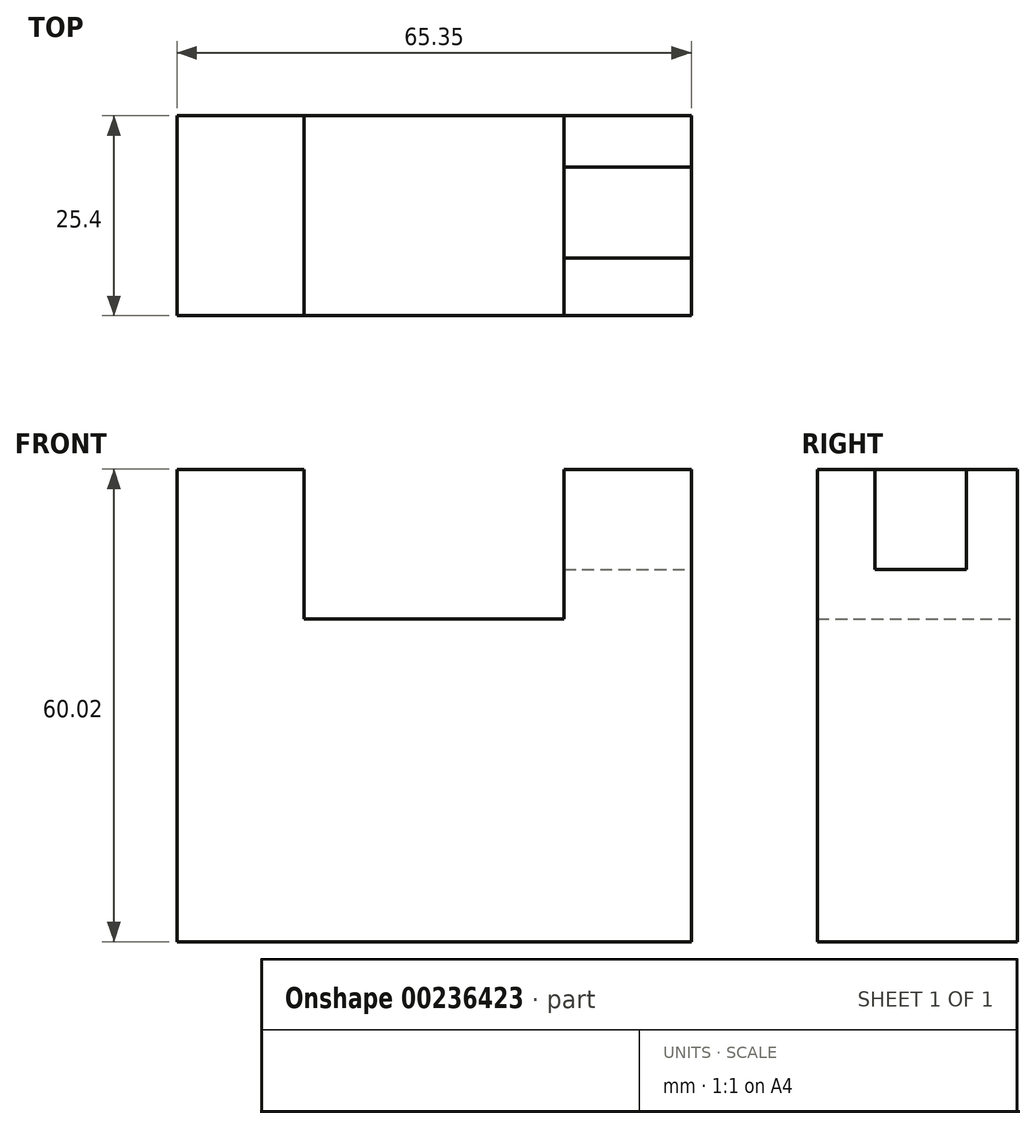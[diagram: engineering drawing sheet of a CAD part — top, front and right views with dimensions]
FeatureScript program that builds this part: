
annotation { "Feature Type Name" : "Feature", "Feature Type Description" : "" }
export const myFeature = defineFeature(function(context is Context, id is Id, definition is map)
    precondition{}
    {
        {
            var Q0;
            Q0=qCreatedBy(makeId("Front.planeOp"),FACE);
            var sketch = newSketch(context, id + "F0", { "sketchPlane" : qUnion([Q0])});
            skLineSegment(sketch, "E0.bottom", {"start": v(0, 0) * mm, "end": v(65.35, 0) * mm});
            skLineSegment(sketch, "E0.top", {"start": v(0, 60.02) * mm, "end": v(16.16, 60.02) * mm});
            skLineSegment(sketch, "E0.left", {"start": v(0, 0) * mm, "end": v(0, 60.02) * mm});
            skLineSegment(sketch, "E0.right", {"start": v(65.35, 0) * mm, "end": v(65.35, 60.02) * mm});
            skLineSegment(sketch, "E1.top", {"start": v(16.16, 40.99) * mm, "end": v(49.18, 40.99) * mm});
            skLineSegment(sketch, "E1.left", {"start": v(16.16, 60.02) * mm, "end": v(16.16, 40.99) * mm});
            skLineSegment(sketch, "E1.right", {"start": v(49.18, 60.02) * mm, "end": v(49.18, 40.99) * mm});
            skLineSegment(sketch, "E2.trimOffspring", {"start": v(49.18, 60.02) * mm, "end": v(65.35, 60.02) * mm});
            skSolve(sketch);
        }
        {
            var Q0;
            Q0=makeQuery(id+"F0.imprint","IMPRINT",FACE,{"disambiguationData":[TD([[makeQuery(id+"F0.imprint","IMPRINT",EDGE,{"derivedFrom":sQuery(id+"F0.wireOp",EDGE,"E0.bottom")}),1.0]])]});
            extrude(context, id + "F1", {"entities" : qUnion([Q0]), "depth" : 25.4 * mm});
        }
        {
            var Q0;
            Q0=makeQuery(id+"F1.opExtrude","SWEPT_FACE",FACE,{"disambiguationData":[OSD([sQuery(id+"F0.wireOp",EDGE,"E2.trimOffspring")])]});
            var sketch = newSketch(context, id + "F2", { "sketchPlane" : qUnion([Q0])});
            skLineSegment(sketch, "E3.bottom", {"start": v(49.18, -18.1) * mm, "end": v(65.35, -18.1) * mm});
            skLineSegment(sketch, "E3.top", {"start": v(49.18, -6.5) * mm, "end": v(65.35, -6.5) * mm});
            skLineSegment(sketch, "E3.left", {"start": v(49.18, -18.1) * mm, "end": v(49.18, -6.5) * mm});
            skLineSegment(sketch, "E3.right", {"start": v(65.35, -18.1) * mm, "end": v(65.35, -6.5) * mm});
            skSolve(sketch);
        }
        {
            var Q0;
            Q0 = qSketchRegion(id + "F2", true);
            extrude(context, id + "F3", {"entities" : qUnion([Q0]), "operationType" : NewBodyOperationType.REMOVE, "oppositeDirection" : true, "depth" : 12.7 * mm});
        }
    });
